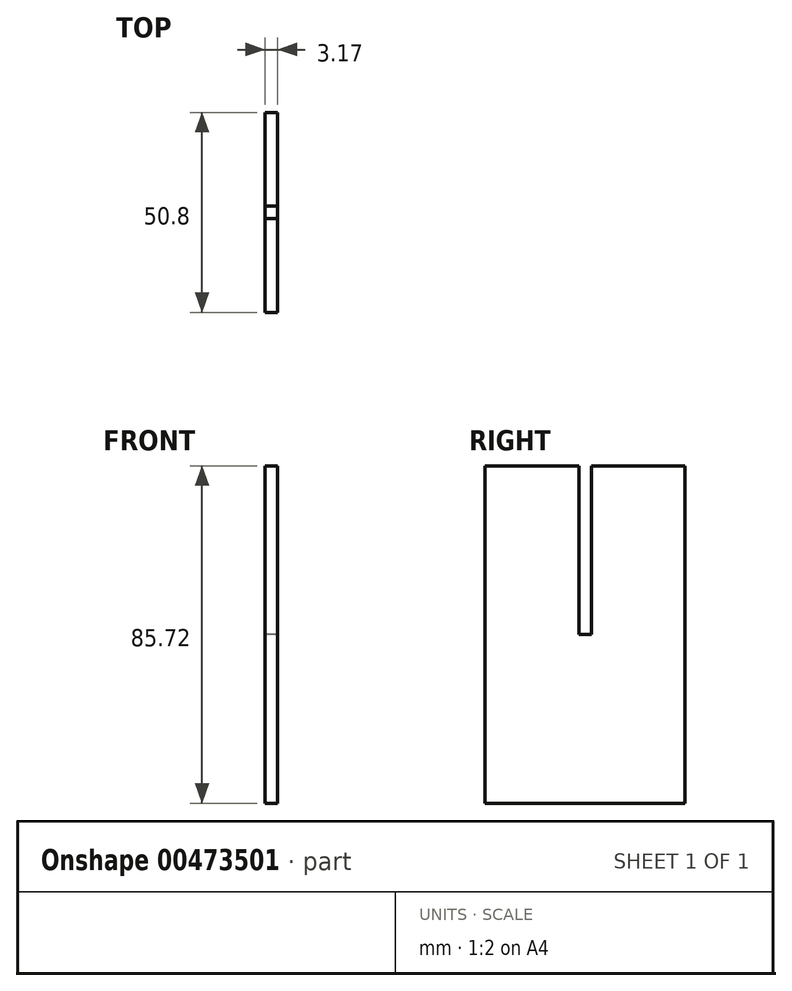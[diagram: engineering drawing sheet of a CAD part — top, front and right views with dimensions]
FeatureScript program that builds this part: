
annotation { "Feature Type Name" : "Feature", "Feature Type Description" : "" }
export const myFeature = defineFeature(function(context is Context, id is Id, definition is map)
    precondition{}
    {
        {
            var Q0;
            Q0=qCreatedBy(makeId("Right.planeOp"),FACE);
            var sketch = newSketch(context, id + "F0", { "sketchPlane" : qUnion([Q0])});
            skLineSegment(sketch, "E0.bottom", {"start": v(25.4, 42.86) * mm, "end": v(1.59, 42.86) * mm});
            skLineSegment(sketch, "E0.top", {"start": v(25.4, -42.86) * mm, "end": v(-25.4, -42.86) * mm});
            skLineSegment(sketch, "E0.left", {"start": v(25.4, 42.86) * mm, "end": v(25.4, -42.86) * mm});
            skLineSegment(sketch, "E0.right", {"start": v(-25.4, 42.86) * mm, "end": v(-25.4, -42.86) * mm});
            skPoint(sketch, "E0.middle", {"position": v(0, 0) * mm});
            skLineSegment(sketch, "E1", {"start": v(-25.4, 42.86) * mm, "end": v(-1.59, 42.86) * mm});
            skLineSegment(sketch, "E2", {"start": v(-1.59, 42.86) * mm, "end": v(-1.59, 0) * mm});
            skLineSegment(sketch, "E3", {"start": v(-1.59, 0) * mm, "end": v(1.59, 0) * mm});
            skLineSegment(sketch, "E4", {"start": v(1.59, 42.86) * mm, "end": v(1.59, 0) * mm});
            skLineSegment(sketch, "E5.trimOffspring", {"start": v(-1.59, 42.86) * mm, "end": v(-25.4, 42.86) * mm});
            skSolve(sketch);
        }
        {
            var Q0;
            Q0 = qSketchRegion(id + "F0", true);
            extrude(context, id + "F1", {"entities" : qUnion([Q0]), "depth" : 3.17 * mm});
        }
    });
